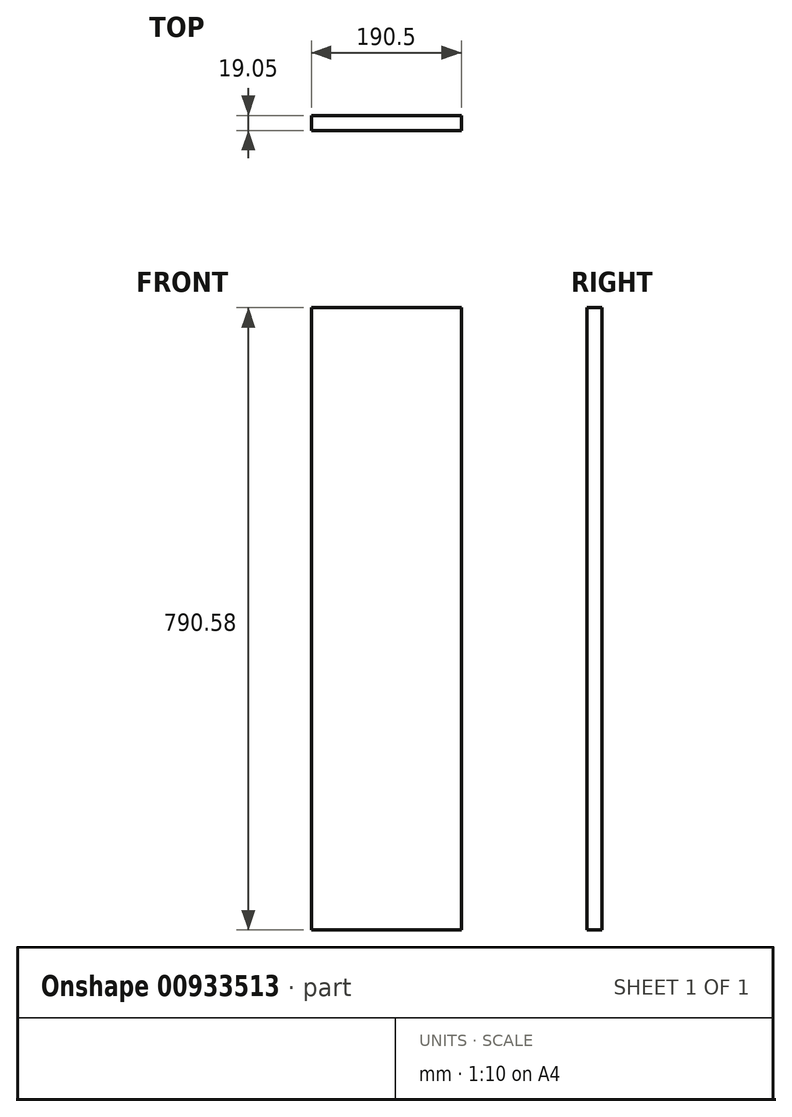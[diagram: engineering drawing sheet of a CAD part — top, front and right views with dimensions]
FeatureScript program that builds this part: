
annotation { "Feature Type Name" : "Feature", "Feature Type Description" : "" }
export const myFeature = defineFeature(function(context is Context, id is Id, definition is map)
    precondition{}
    {
        {
            var Q0;
            Q0=qCreatedBy(makeId("Top.planeOp"),FACE);
            var sketch = newSketch(context, id + "F0", { "sketchPlane" : qUnion([Q0])});
            skLineSegment(sketch, "E0.bottom", {"start": v(0, 0) * mm, "end": v(190.5, 0) * mm});
            skLineSegment(sketch, "E0.top", {"start": v(0, 19.05) * mm, "end": v(190.5, 19.05) * mm});
            skLineSegment(sketch, "E0.left", {"start": v(0, 0) * mm, "end": v(0, 19.05) * mm});
            skLineSegment(sketch, "E0.right", {"start": v(190.5, 0) * mm, "end": v(190.5, 19.05) * mm});
            skSolve(sketch);
        }
        {
            var Q0;
            Q0 = qSketchRegion(id + "F0", true);
            extrude(context, id + "F1", {"entities" : qUnion([Q0]), "depth" : 790.57 * mm, "offsetDistance" : 25.4 * mm});
        }
    });
